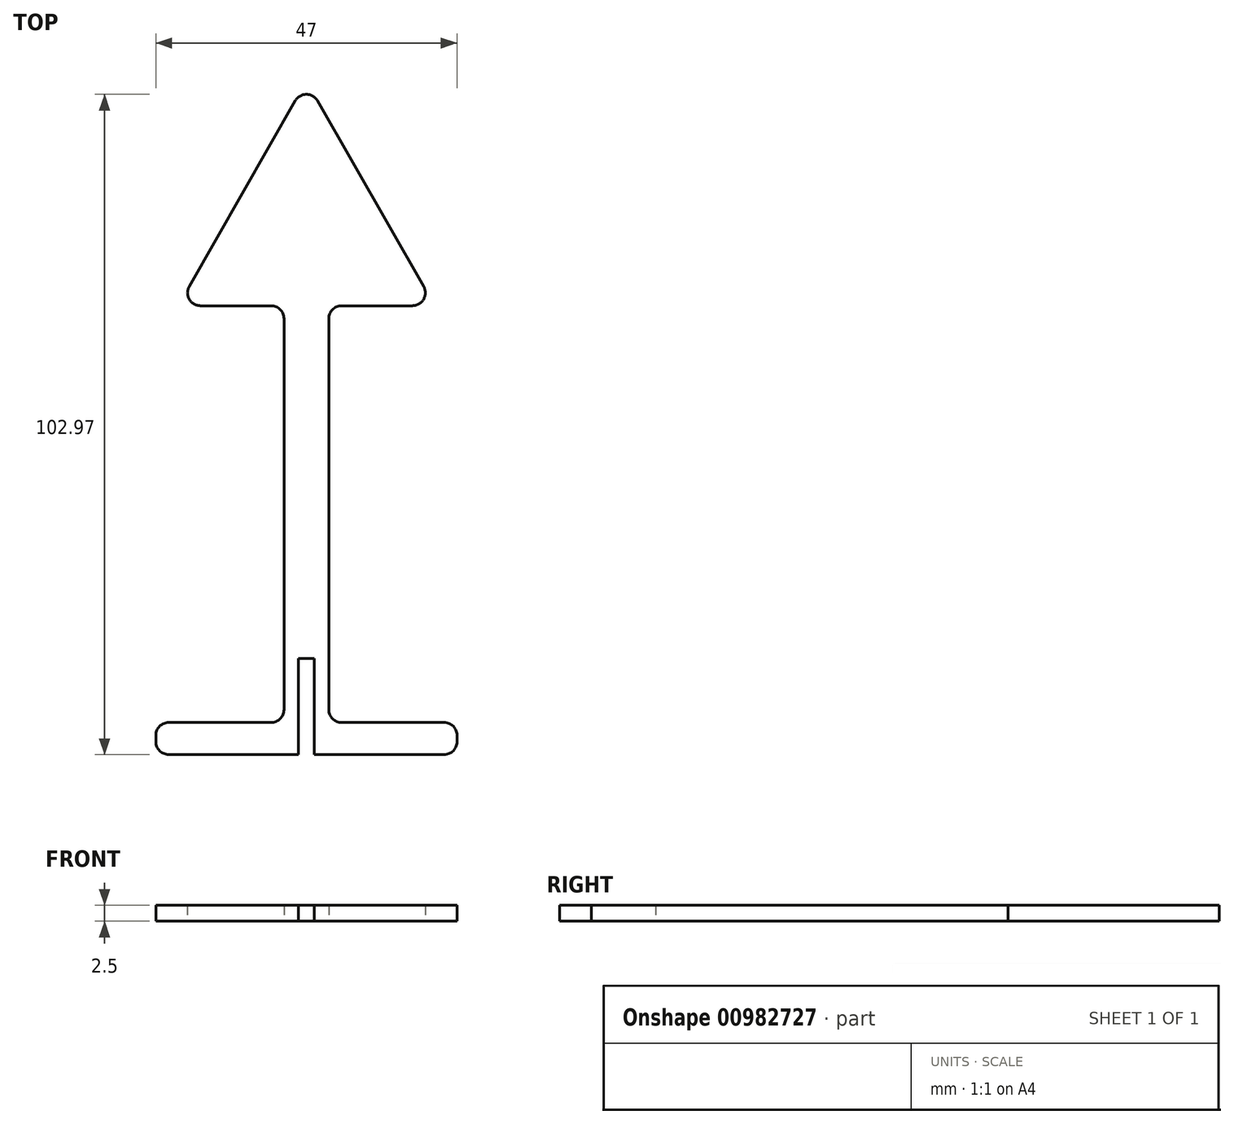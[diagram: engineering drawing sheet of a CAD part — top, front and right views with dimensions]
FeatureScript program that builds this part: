
annotation { "Feature Type Name" : "Feature", "Feature Type Description" : "" }
export const myFeature = defineFeature(function(context is Context, id is Id, definition is map)
    precondition{}
    {
        {
            var Q0;
            Q0=qCreatedBy(makeId("Top.planeOp"),FACE);
            var sketch = newSketch(context, id + "F0", { "sketchPlane" : qUnion([Q0])});
            skLineSegment(sketch, "E0", {"start": v(-20, 0) * mm, "end": v(20, 0) * mm});
            skLineSegment(sketch, "E1", {"start": v(20, 0) * mm, "end": v(0, 35) * mm});
            skLineSegment(sketch, "E2", {"start": v(0, 35) * mm, "end": v(-20, 0) * mm});
            skPoint(sketch, "E3", {"position": v(0, 0) * mm});
            skLineSegment(sketch, "E4", {"start": v(-3.5, 0) * mm, "end": v(-3.5, -65) * mm});
            skLineSegment(sketch, "E5", {"start": v(-3.5, -65) * mm, "end": v(-23.5, -65) * mm});
            skLineSegment(sketch, "E6", {"start": v(-23.5, -65) * mm, "end": v(-23.5, -70) * mm});
            skLineSegment(sketch, "E7", {"start": v(-23.5, -70) * mm, "end": v(23.5, -70) * mm});
            skLineSegment(sketch, "E8", {"start": v(23.5, -70) * mm, "end": v(23.5, -65) * mm});
            skLineSegment(sketch, "E9", {"start": v(23.5, -65) * mm, "end": v(3.5, -65) * mm});
            skLineSegment(sketch, "E10", {"start": v(3.5, -65) * mm, "end": v(3.5, 0) * mm});
            skLineSegment(sketch, "E11.bottom", {"start": v(1.25, -70) * mm, "end": v(-1.25, -70) * mm});
            skLineSegment(sketch, "E11.top", {"start": v(1.25, -55) * mm, "end": v(-1.25, -55) * mm});
            skLineSegment(sketch, "E11.left", {"start": v(1.25, -70) * mm, "end": v(1.25, -55) * mm});
            skLineSegment(sketch, "E11.right", {"start": v(-1.25, -70) * mm, "end": v(-1.25, -55) * mm});
            skPoint(sketch, "E11.middle", {"position": v(0, -62.5) * mm});
            skLineSegment(sketch, "E12.bottom", {"start": v(-23.5, -70) * mm, "end": v(-17.5, -70) * mm});
            skLineSegment(sketch, "E12.top", {"start": v(-23.5, -70.3) * mm, "end": v(-17.5, -70.3) * mm});
            skLineSegment(sketch, "E12.left", {"start": v(-23.5, -70) * mm, "end": v(-23.5, -70.3) * mm});
            skLineSegment(sketch, "E12.right", {"start": v(-17.5, -70) * mm, "end": v(-17.5, -70.3) * mm});
            skLineSegment(sketch, "E13.MirrorCS", {"start": v(23.5, -70) * mm, "end": v(17.5, -70) * mm});
            skLineSegment(sketch, "E14.MirrorCS", {"start": v(17.5, -70) * mm, "end": v(17.5, -70.3) * mm});
            skLineSegment(sketch, "E15.MirrorCS", {"start": v(23.5, -70.3) * mm, "end": v(17.5, -70.3) * mm});
            skLineSegment(sketch, "E16.MirrorCS", {"start": v(23.5, -70) * mm, "end": v(23.5, -70.3) * mm});
            skSolve(sketch);
        }
        {
            var Q0;
            {var subQ0=sQuery(id+"F0.wireOp",EDGE,"E1");Q0=makeQuery(id+"F0.imprint","IMPRINT",FACE,{"disambiguationData":[TD([[makeQuery(id+"F0.imprint","IMPRINT",EDGE,{"derivedFrom":subQ0}),1.0]])]});}
            var Q1;
            {var subQ7=sQuery(id+"F0.wireOp",EDGE,"E4");Q1=makeQuery(id+"F0.imprint","IMPRINT",FACE,{"disambiguationData":[TD([[makeQuery(id+"F0.imprint","IMPRINT",EDGE,{"derivedFrom":subQ7}),1.0]])]});}
            var Q2;
            Q2=makeQuery(id+"F0.imprint","IMPRINT",FACE,{"disambiguationData":[TD([[makeQuery(id+"F0.imprint","IMPRINT",EDGE,{"derivedFrom":sQuery(id+"F0.wireOp",EDGE,"E12.bottom")}),-1.0]])]});
            var Q3;
            Q3=makeQuery(id+"F0.imprint","IMPRINT",FACE,{"disambiguationData":[TD([[makeQuery(id+"F0.imprint","IMPRINT",EDGE,{"derivedFrom":sQuery(id+"F0.wireOp",EDGE,"E13.MirrorCS")}),1.0]])]});
            extrude(context, id + "F1", {"entities" : qUnion([Q0, Q1, Q2, Q3]), "flatOperationType" : FlatOperationType.REMOVE, "depth" : 2.5 * mm, "offsetDistance" : 25 * mm, "domain" : OperationDomain.MODEL});
        }
        {
            var Q0;
            Q0=makeQuery(id+"F1.opExtrude","SWEPT_EDGE",EDGE,{"disambiguationData":[OSD([sQuery(id+"F0.wireOp",EDGE,"E0"),sQuery(id+"F0.wireOp",EDGE,"E4")])]});
            var Q1;
            Q1=makeQuery(id+"F1.opExtrude","SWEPT_EDGE",EDGE,{"disambiguationData":[OSD([sQuery(id+"F0.wireOp",EDGE,"E0"),sQuery(id+"F0.wireOp",EDGE,"E10")])]});
            var Q2;
            Q2=makeQuery(id+"F1.opExtrude","SWEPT_EDGE",EDGE,{"disambiguationData":[OSD([sQuery(id+"F0.wireOp",EDGE,"E0"),sQuery(id+"F0.wireOp",EDGE,"E1")])]});
            var Q3;
            Q3=makeQuery(id+"F1.opExtrude","SWEPT_EDGE",EDGE,{"disambiguationData":[OSD([sQuery(id+"F0.wireOp",EDGE,"E0"),sQuery(id+"F0.wireOp",EDGE,"E2")])]});
            var Q4;
            Q4=makeQuery(id+"F1.opExtrude","SWEPT_EDGE",EDGE,{"disambiguationData":[OSD([sQuery(id+"F0.wireOp",EDGE,"E1"),sQuery(id+"F0.wireOp",EDGE,"E2")])]});
            var Q5;
            Q5=makeQuery(id+"F1.opExtrude","SWEPT_EDGE",EDGE,{"disambiguationData":[OSD([sQuery(id+"F0.wireOp",EDGE,"E9"),sQuery(id+"F0.wireOp",EDGE,"E10")])]});
            var Q6;
            Q6=makeQuery(id+"F1.opExtrude","SWEPT_EDGE",EDGE,{"disambiguationData":[OSD([sQuery(id+"F0.wireOp",EDGE,"E4"),sQuery(id+"F0.wireOp",EDGE,"E5")])]});
            var Q7;
            Q7=makeQuery(id+"F1.opExtrude","SWEPT_EDGE",EDGE,{"disambiguationData":[OSD([sQuery(id+"F0.wireOp",EDGE,"E5"),sQuery(id+"F0.wireOp",EDGE,"E6")])]});
            var Q8;
            Q8=makeQuery(id+"F1.opExtrude","SWEPT_EDGE",EDGE,{"disambiguationData":[OSD([sQuery(id+"F0.wireOp",EDGE,"E8"),sQuery(id+"F0.wireOp",EDGE,"E9")])]});
            var Q9;
            Q9=makeQuery(id+"F1.opExtrude","SWEPT_EDGE",EDGE,{"disambiguationData":[OSD([sQuery(id+"F0.wireOp",EDGE,"E12.top"),sQuery(id+"F0.wireOp",EDGE,"E12.left")])]});
            var Q10;
            Q10=makeQuery(id+"F1.opExtrude","SWEPT_EDGE",EDGE,{"disambiguationData":[OSD([sQuery(id+"F0.wireOp",EDGE,"E15.MirrorCS"),sQuery(id+"F0.wireOp",EDGE,"E16.MirrorCS")])]});
            fillet(context, id + "F2", {"entities" : qUnion([Q0, Q1, Q2, Q3, Q4, Q5, Q6, Q7, Q8, Q9, Q10]), "radius" : 2 * mm, "tangentPropagation" : true, "allowEdgeOverflow" : false});
        }
    });
